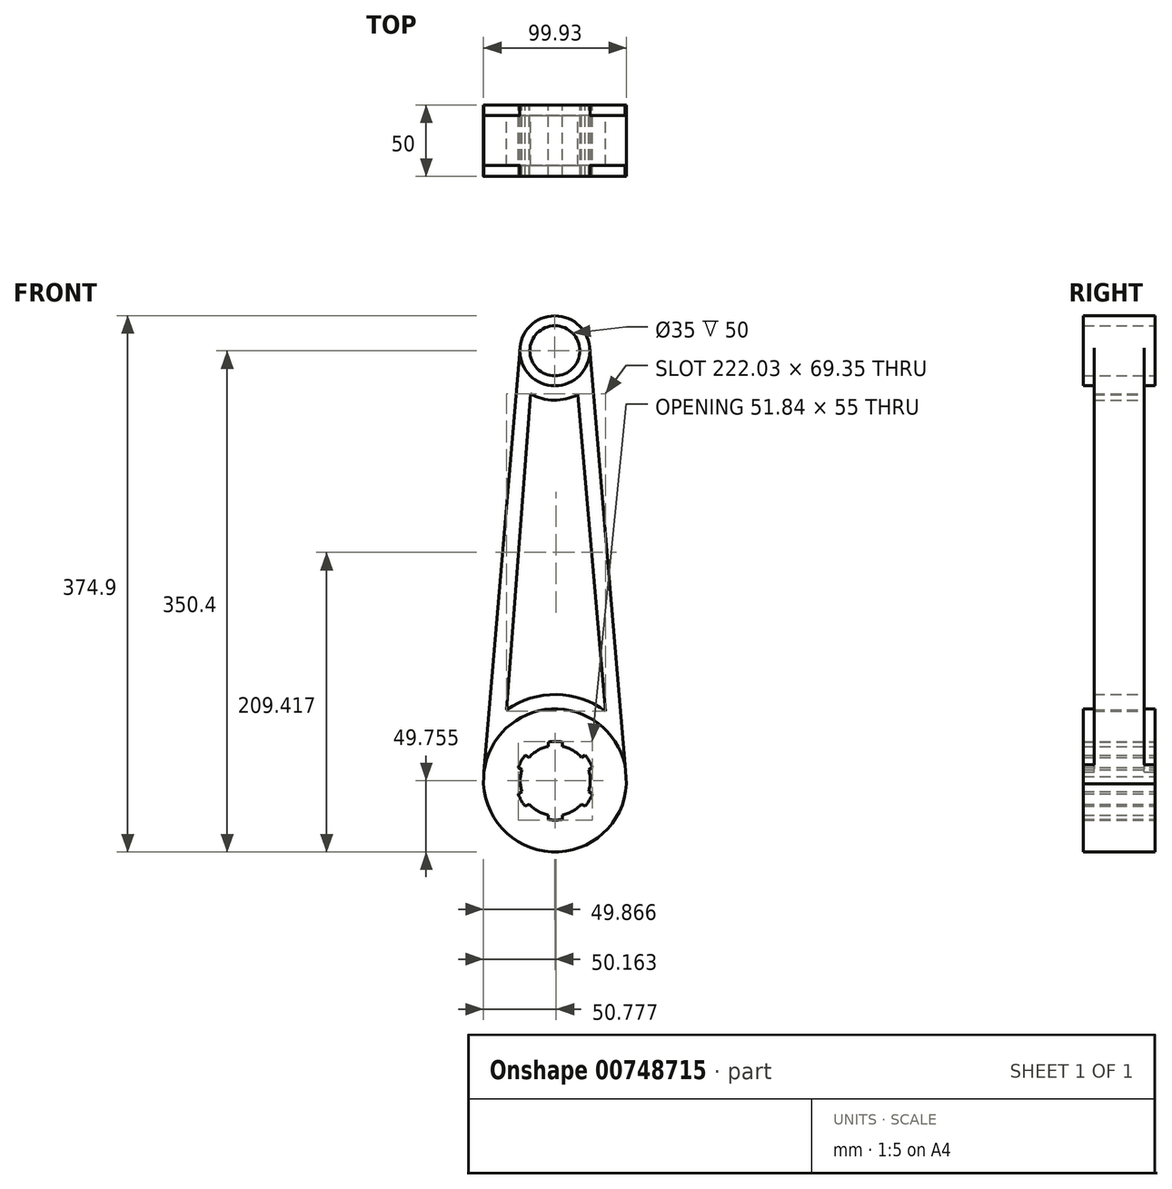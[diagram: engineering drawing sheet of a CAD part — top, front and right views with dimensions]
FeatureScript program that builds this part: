
annotation { "Feature Type Name" : "Feature", "Feature Type Description" : "" }
export const myFeature = defineFeature(function(context is Context, id is Id, definition is map)
    precondition{}
    {
        {
            var Q0;
            Q0=qCreatedBy(makeId("Front.planeOp"),FACE);
            var sketch = newSketch(context, id + "F0", { "sketchPlane" : qUnion([Q0])});
            skCircle(sketch, "E0", {"center": v(0, 0) * mm, "radius": 50 * mm});
            skCircle(sketch, "E1", {"center": v(-0.13, 300.4) * mm, "radius": 17.5 * mm});
            skCircle(sketch, "E2", {"center": v(-0.13, 300.4) * mm, "radius": 24.5 * mm});
            skLineSegment(sketch, "E3", {"start": v(49.93, -2.56) * mm, "end": v(24.28, 302.45) * mm});
            skLineSegment(sketch, "E4", {"start": v(-49.93, 2.56) * mm, "end": v(-24.55, 302.47) * mm});
            skArc(sketch, "E5.0", {"start": v(35.45, 48.4) * mm, "mid": v(0.95, 60) * mm, "end": v(-33.9, 49.5) * mm});
            skArc(sketch, "E6.0", {"start": v(-17.22, 270.43) * mm, "mid": v(-0.76, 265.9) * mm, "end": v(15.85, 269.83) * mm});
            skLineSegment(sketch, "E7.trimOffspring", {"start": v(-33.9, 49.5) * mm, "end": v(-17.22, 270.43) * mm});
            skLineSegment(sketch, "E8.trimOffspring", {"start": v(35.45, 48.4) * mm, "end": v(15.85, 269.83) * mm});
            skArc(sketch, "E9", {"start": v(-23.1, 7.42) * mm, "mid": v(-24.34, -0.24) * mm, "end": v(-23.1, -7.9) * mm});
            skLineSegment(sketch, "E10", {"start": v(5.16, 26.8) * mm, "end": v(5.16, 23.74) * mm});
            skLineSegment(sketch, "E11", {"start": v(-4.84, 26.8) * mm, "end": v(-4.84, 23.74) * mm});
            skArc(sketch, "E12", {"start": v(-20.76, 17.6) * mm, "mid": v(-23.65, 13.5) * mm, "end": v(-25.76, 8.95) * mm});
            skLineSegment(sketch, "E13", {"start": v(-25.76, 8.95) * mm, "end": v(-25.63, 8.87) * mm});
            skLineSegment(sketch, "E14", {"start": v(-25.63, 8.87) * mm, "end": v(-23.1, 7.42) * mm});
            skLineSegment(sketch, "E15", {"start": v(-20.76, 17.6) * mm, "end": v(-18.1, 16.08) * mm});
            skLineSegment(sketch, "E16", {"start": v(-20.76, -18.1) * mm, "end": v(-18.1, -16.57) * mm});
            skLineSegment(sketch, "E17", {"start": v(-25.76, -9.44) * mm, "end": v(-23.1, -7.9) * mm});
            skArc(sketch, "E18.trimOffspring", {"start": v(-25.76, -9.44) * mm, "mid": v(-23.65, -14) * mm, "end": v(-20.76, -18.1) * mm});
            skLineSegment(sketch, "E19", {"start": v(-4.84, -27.29) * mm, "end": v(-4.84, -24.23) * mm});
            skLineSegment(sketch, "E20", {"start": v(5.16, -27.29) * mm, "end": v(5.16, -24.23) * mm});
            skArc(sketch, "E21.trimOffspring", {"start": v(-4.84, -27.29) * mm, "mid": v(0.16, -27.74) * mm, "end": v(5.16, -27.29) * mm});
            skLineSegment(sketch, "E22", {"start": v(21.08, -18.1) * mm, "end": v(18.43, -16.57) * mm});
            skLineSegment(sketch, "E23", {"start": v(26.08, -9.44) * mm, "end": v(23.43, -7.9) * mm});
            skArc(sketch, "E24.trimOffspring", {"start": v(21.08, -18.1) * mm, "mid": v(23.98, -14) * mm, "end": v(26.08, -9.44) * mm});
            skLineSegment(sketch, "E25", {"start": v(21.08, 17.6) * mm, "end": v(18.43, 16.08) * mm});
            skLineSegment(sketch, "E26", {"start": v(26.08, 8.95) * mm, "end": v(23.43, 7.42) * mm});
            skArc(sketch, "E27.trimOffspring", {"start": v(5.16, 26.8) * mm, "mid": v(0.16, 27.26) * mm, "end": v(-4.84, 26.8) * mm});
            skArc(sketch, "E28.trimOffspring", {"start": v(26.08, 8.95) * mm, "mid": v(23.98, 13.5) * mm, "end": v(21.08, 17.6) * mm});
            skArc(sketch, "E29.trimOffspring", {"start": v(-4.84, 23.74) * mm, "mid": v(-12.09, 20.97) * mm, "end": v(-18.1, 16.08) * mm});
            skArc(sketch, "E30.trimOffspring", {"start": v(18.43, 16.08) * mm, "mid": v(12.41, 20.97) * mm, "end": v(5.16, 23.74) * mm});
            skArc(sketch, "E31.trimOffspring", {"start": v(23.43, -7.9) * mm, "mid": v(24.66, -0.24) * mm, "end": v(23.43, 7.42) * mm});
            skArc(sketch, "E32.trimOffspring", {"start": v(-18.1, -16.57) * mm, "mid": v(-12.09, -21.46) * mm, "end": v(-4.84, -24.23) * mm});
            skArc(sketch, "E33.trimOffspring", {"start": v(5.16, -24.23) * mm, "mid": v(12.41, -21.46) * mm, "end": v(18.43, -16.57) * mm});
            skSolve(sketch);
        }
        {
            var Q0;
            Q0=makeQuery(id+"F0.imprint","IMPRINT",FACE,{"disambiguationData":[TD([[makeQuery(id+"F0.imprint","IMPRINT",EDGE,{"derivedFrom":sQuery(id+"F0.wireOp",EDGE,"E5.0")}),1.0]])]});
            extrude(context, id + "F1", {"entities" : qUnion([Q0]), "endBound" : BoundingType.SYMMETRIC, "depth" : 35 * mm, "offsetDistance" : 25 * mm});
        }
        {
            var Q0;
            Q0=makeQuery(id+"F0.imprint","IMPRINT",FACE,{"disambiguationData":[TD([[makeQuery(id+"F0.imprint","IMPRINT",EDGE,{"derivedFrom":sQuery(id+"F0.wireOp",EDGE,"E1")}),-1.0]])]});
            var Q1;
            Q1=makeQuery(id+"F0.imprint","IMPRINT",FACE,{"disambiguationData":[TD([[makeQuery(id+"F0.imprint","IMPRINT",EDGE,{"derivedFrom":sQuery(id+"F0.wireOp",EDGE,"E9")}),-1.0]])]});
            extrude(context, id + "F2", {"entities" : qUnion([Q0, Q1]), "operationType" : NewBodyOperationType.ADD, "endBound" : BoundingType.SYMMETRIC, "depth" : 50 * mm, "offsetDistance" : 25 * mm});
        }
    });
